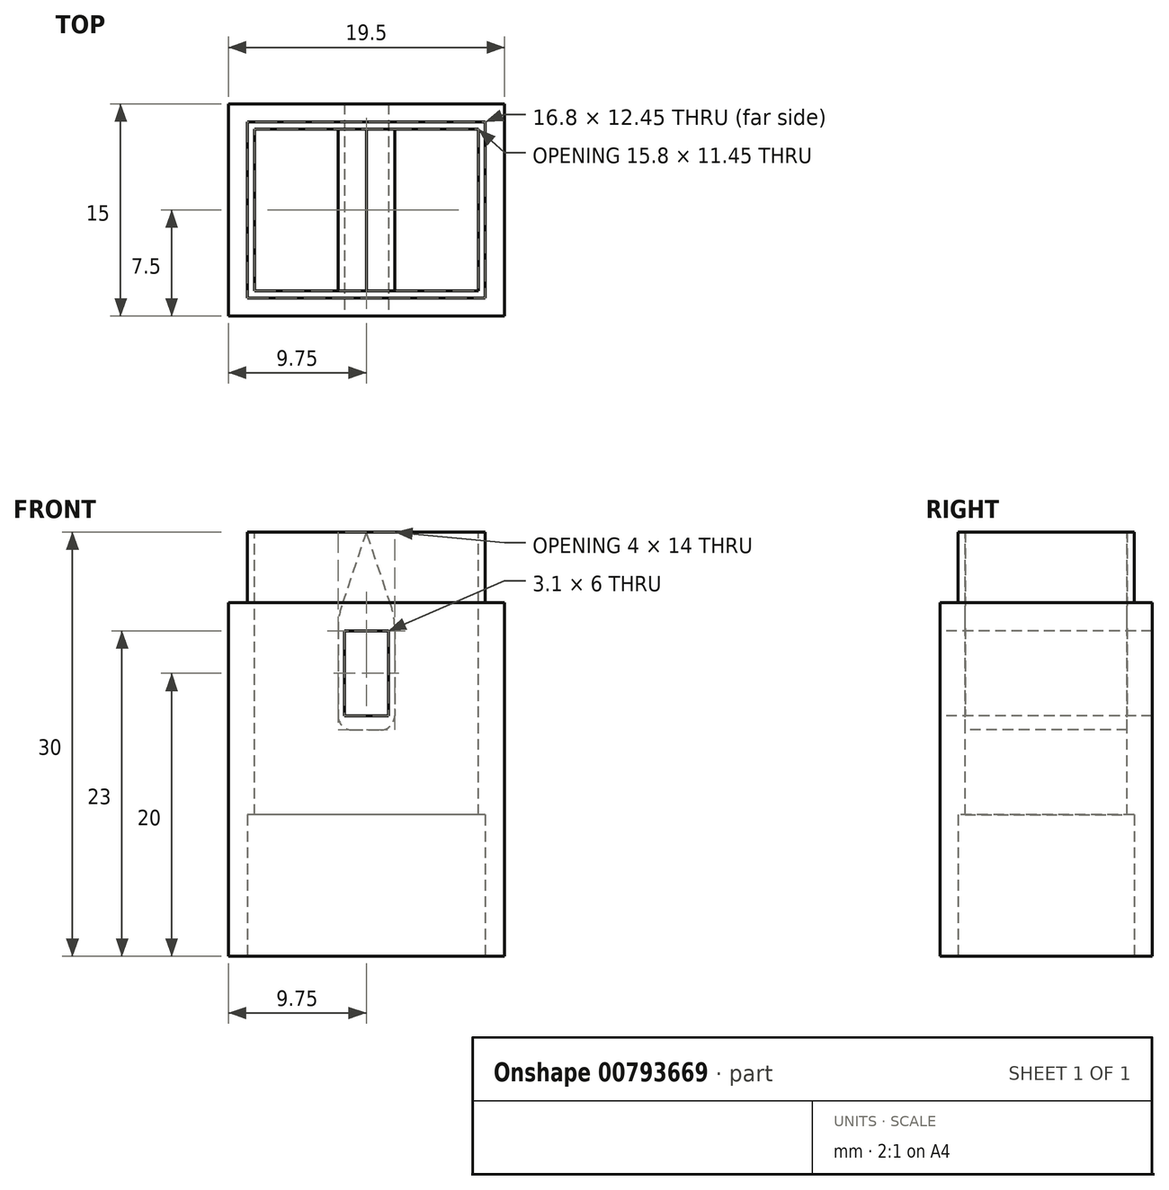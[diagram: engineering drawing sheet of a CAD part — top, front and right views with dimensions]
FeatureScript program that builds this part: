
annotation { "Feature Type Name" : "Feature", "Feature Type Description" : "" }
export const myFeature = defineFeature(function(context is Context, id is Id, definition is map)
    precondition{}
    {
        {
            var Q0;
            Q0=qCreatedBy(makeId("Front.planeOp"),FACE);
            var sketch = newSketch(context, id + "F0", { "sketchPlane" : qUnion([Q0])});
            skLineSegment(sketch, "E0.bottom", {"start": v(9.75, -15) * mm, "end": v(-9.75, -15) * mm});
            skLineSegment(sketch, "E0.top", {"start": v(9.75, 15) * mm, "end": v(-9.75, 15) * mm});
            skLineSegment(sketch, "E0.left", {"start": v(9.75, -15) * mm, "end": v(9.75, 15) * mm});
            skLineSegment(sketch, "E0.right", {"start": v(-9.75, -15) * mm, "end": v(-9.75, 15) * mm});
            skPoint(sketch, "E0.middle", {"position": v(0, 0) * mm});
            skSolve(sketch);
        }
        {
            var Q0;
            Q0 = qSketchRegion(id + "F0", true);
            extrude(context, id + "F1", {"entities" : qUnion([Q0]), "depth" : 15 * mm, "offsetDistance" : 25 * mm});
        }
        {
            var Q0;
            Q0=makeQuery(id+"F1.opExtrude","SWEPT_FACE",FACE,{"disambiguationData":[OSD([sQuery(id+"F0.wireOp",EDGE,"E0.top")])]});
            var sketch = newSketch(context, id + "F2", { "sketchPlane" : qUnion([Q0])});
            skLineSegment(sketch, "E1", {"start": v(-9.75, 0) * mm, "end": v(9.75, -15) * mm, "construction": true});
            skLineSegment(sketch, "E2.bottom", {"start": v(7.9, -13.23) * mm, "end": v(-7.9, -13.23) * mm});
            skLineSegment(sketch, "E2.top", {"start": v(7.9, -1.77) * mm, "end": v(-7.9, -1.77) * mm});
            skLineSegment(sketch, "E2.left", {"start": v(7.9, -13.23) * mm, "end": v(7.9, -1.77) * mm});
            skLineSegment(sketch, "E2.right", {"start": v(-7.9, -13.23) * mm, "end": v(-7.9, -1.77) * mm});
            skPoint(sketch, "E2.middle", {"position": v(0, -7.5) * mm});
            skSolve(sketch);
        }
        {
            var Q0;
            Q0 = qSketchRegion(id + "F2", true);
            extrude(context, id + "F3", {"entities" : qUnion([Q0]), "operationType" : NewBodyOperationType.REMOVE, "endBound" : BoundingType.UP_TO_NEXT, "oppositeDirection" : true, "depth" : 25 * mm, "offsetDistance" : 25 * mm});
        }
        {
            var Q0;
            Q0=makeQuery(id+"F1.opExtrude","CAP_FACE",FACE,{"disambiguationData":[OSD([sQuery(id+"F0.wireOp",EDGE,"E0.bottom"),sQuery(id+"F0.wireOp",EDGE,"E0.top"),sQuery(id+"F0.wireOp",EDGE,"E0.left"),sQuery(id+"F0.wireOp",EDGE,"E0.right")])],"isStart":false});
            var sketch = newSketch(context, id + "F4", { "sketchPlane" : qUnion([Q0])});
            skLineSegment(sketch, "E3.bottom", {"start": v(2, 1) * mm, "end": v(-2, 1) * mm});
            skLineSegment(sketch, "E3.left", {"start": v(2, 1) * mm, "end": v(2, 9) * mm});
            skLineSegment(sketch, "E3.right", {"start": v(-2, 1) * mm, "end": v(-2, 9) * mm});
            skPoint(sketch, "E3.middle", {"position": v(0, 5) * mm});
            skPoint(sketch, "E3.middle.positionSnap0", {"position": v(0, 15) * mm});
            skPoint(sketch, "E3.centerSnap0", {"position": v(0, 15) * mm});
            skLineSegment(sketch, "E4", {"start": v(-2, 9) * mm, "end": v(0, 15) * mm});
            skLineSegment(sketch, "E5", {"start": v(0, 15) * mm, "end": v(2, 9) * mm});
            skSolve(sketch);
        }
        {
            var Q0;
            Q0 = qSketchRegion(id + "F4", true);
            var Q1;
            Q1=makeQuery(id+"F1.opExtrude","CAP_FACE",FACE,{"disambiguationData":[OSD([sQuery(id+"F0.wireOp",EDGE,"E0.bottom"),sQuery(id+"F0.wireOp",EDGE,"E0.top"),sQuery(id+"F0.wireOp",EDGE,"E0.left"),sQuery(id+"F0.wireOp",EDGE,"E0.right")])],"isStart":true});
            extrude(context, id + "F5", {"entities" : qUnion([Q0]), "operationType" : NewBodyOperationType.ADD, "endBound" : BoundingType.UP_TO_SURFACE, "oppositeDirection" : true, "depth" : 25 * mm, "endBoundEntityFace" : qUnion([Q1]), "offsetDistance" : 25 * mm});
        }
        {
            var Q0;
            Q0=makeQuery(id+"F1.opExtrude","CAP_FACE",FACE,{"disambiguationData":[OSD([sQuery(id+"F0.wireOp",EDGE,"E0.bottom"),sQuery(id+"F0.wireOp",EDGE,"E0.top"),sQuery(id+"F0.wireOp",EDGE,"E0.left"),sQuery(id+"F0.wireOp",EDGE,"E0.right")])],"isStart":false});
            var sketch = newSketch(context, id + "F6", { "sketchPlane" : qUnion([Q0])});
            skLineSegment(sketch, "E6.bottom", {"start": v(1.55, 2) * mm, "end": v(-1.55, 2) * mm});
            skLineSegment(sketch, "E6.top", {"start": v(1.55, 8) * mm, "end": v(-1.55, 8) * mm});
            skLineSegment(sketch, "E6.left", {"start": v(1.55, 2) * mm, "end": v(1.55, 8) * mm});
            skLineSegment(sketch, "E6.right", {"start": v(-1.55, 2) * mm, "end": v(-1.55, 8) * mm});
            skPoint(sketch, "E6.middle", {"position": v(0, 5) * mm});
            skPoint(sketch, "E6.middle.positionSnap0", {"position": v(0, 15) * mm});
            skPoint(sketch, "E6.centerSnap0", {"position": v(0, 15) * mm});
            skSolve(sketch);
        }
        {
            var Q0;
            Q0 = qSketchRegion(id + "F6", true);
            extrude(context, id + "F7", {"entities" : qUnion([Q0]), "operationType" : NewBodyOperationType.REMOVE, "endBound" : BoundingType.UP_TO_NEXT, "oppositeDirection" : true, "depth" : 25 * mm, "offsetDistance" : 25 * mm});
        }
        {
            var Q0;
            Q0=makeQuery(id+"F5.opExtrude","SWEPT_EDGE",EDGE,{"disambiguationData":[OSD([sQuery(id+"F4.wireOp",EDGE,"E3.right"),sQuery(id+"F4.wireOp",EDGE,"E4")])]});
            var Q1;
            Q1=makeQuery(id+"F5.opExtrude","SWEPT_EDGE",EDGE,{"disambiguationData":[OSD([sQuery(id+"F4.wireOp",EDGE,"E3.left"),sQuery(id+"F4.wireOp",EDGE,"E5")])]});
            fillet(context, id + "F8", {"entities" : qUnion([Q0, Q1]), "radius" : 5 * mm, "tangentPropagation" : true, "allowEdgeOverflow" : false});
        }
        {
            var Q0;
            Q0=makeQuery(id+"F5.opExtrude","SWEPT_EDGE",EDGE,{"disambiguationData":[OSD([sQuery(id+"F4.wireOp",EDGE,"E3.bottom"),sQuery(id+"F4.wireOp",EDGE,"E3.right")])]});
            var Q1;
            Q1=makeQuery(id+"F5.opExtrude","SWEPT_EDGE",EDGE,{"disambiguationData":[OSD([sQuery(id+"F4.wireOp",EDGE,"E3.bottom"),sQuery(id+"F4.wireOp",EDGE,"E3.left")])]});
            fillet(context, id + "F9", {"entities" : qUnion([Q0, Q1]), "radius" : 1 * mm, "tangentPropagation" : true, "allowEdgeOverflow" : false});
        }
        {
            var Q0;
            Q0=makeQuery(id+"F1.opExtrude","SWEPT_FACE",FACE,{"disambiguationData":[OSD([sQuery(id+"F0.wireOp",EDGE,"E0.top")])]});
            var sketch = newSketch(context, id + "F10", { "sketchPlane" : qUnion([Q0])});
            skLineSegment(sketch, "E7", {"start": v(-9.75, 0) * mm, "end": v(9.75, -15) * mm, "construction": true});
            skLineSegment(sketch, "E8.bottom", {"start": v(8.4, -13.72) * mm, "end": v(-8.4, -13.73) * mm});
            skLineSegment(sketch, "E8.top", {"start": v(8.4, -1.27) * mm, "end": v(-8.4, -1.28) * mm});
            skLineSegment(sketch, "E8.left", {"start": v(8.4, -13.72) * mm, "end": v(8.4, -1.27) * mm});
            skLineSegment(sketch, "E8.right", {"start": v(-8.4, -13.73) * mm, "end": v(-8.4, -1.28) * mm});
            skPoint(sketch, "E8.middle", {"position": v(0, -7.5) * mm});
            skLineSegment(sketch, "E9.0", {"start": v(9.75, 0) * mm, "end": v(-9.75, 0) * mm});
            skLineSegment(sketch, "E9.1", {"start": v(9.75, -15) * mm, "end": v(9.75, 0) * mm});
            skLineSegment(sketch, "E9.2", {"start": v(9.75, -15) * mm, "end": v(-9.75, -15) * mm});
            skLineSegment(sketch, "E9.3", {"start": v(-9.75, -15) * mm, "end": v(-9.75, 0) * mm});
            skSolve(sketch);
        }
        {
            var Q0;
            Q0 = qSketchRegion(id + "F10", true);
            extrude(context, id + "F11", {"entities" : qUnion([Q0]), "operationType" : NewBodyOperationType.REMOVE, "oppositeDirection" : true, "depth" : 5 * mm, "offsetDistance" : 25 * mm});
        }
        {
            var Q0;
            Q0=makeQuery(id+"F1.opExtrude","SWEPT_FACE",FACE,{"disambiguationData":[OSD([sQuery(id+"F0.wireOp",EDGE,"E0.bottom")])]});
            var sketch = newSketch(context, id + "F12", { "sketchPlane" : qUnion([Q0])});
            skLineSegment(sketch, "E10", {"start": v(-9.75, 15) * mm, "end": v(9.75, 0) * mm, "construction": true});
            skLineSegment(sketch, "E11.bottom", {"start": v(8.4, 1.28) * mm, "end": v(-8.4, 1.27) * mm});
            skLineSegment(sketch, "E11.top", {"start": v(8.4, 13.73) * mm, "end": v(-8.4, 13.72) * mm});
            skLineSegment(sketch, "E11.left", {"start": v(8.4, 1.28) * mm, "end": v(8.4, 13.73) * mm});
            skLineSegment(sketch, "E11.right", {"start": v(-8.4, 1.27) * mm, "end": v(-8.4, 13.73) * mm});
            skPoint(sketch, "E11.middle", {"position": v(0, 7.5) * mm});
            skSolve(sketch);
        }
        {
            var Q0;
            Q0 = qSketchRegion(id + "F12", true);
            extrude(context, id + "F13", {"entities" : qUnion([Q0]), "operationType" : NewBodyOperationType.REMOVE, "oppositeDirection" : true, "depth" : 10 * mm, "offsetDistance" : 25 * mm});
        }
    });
